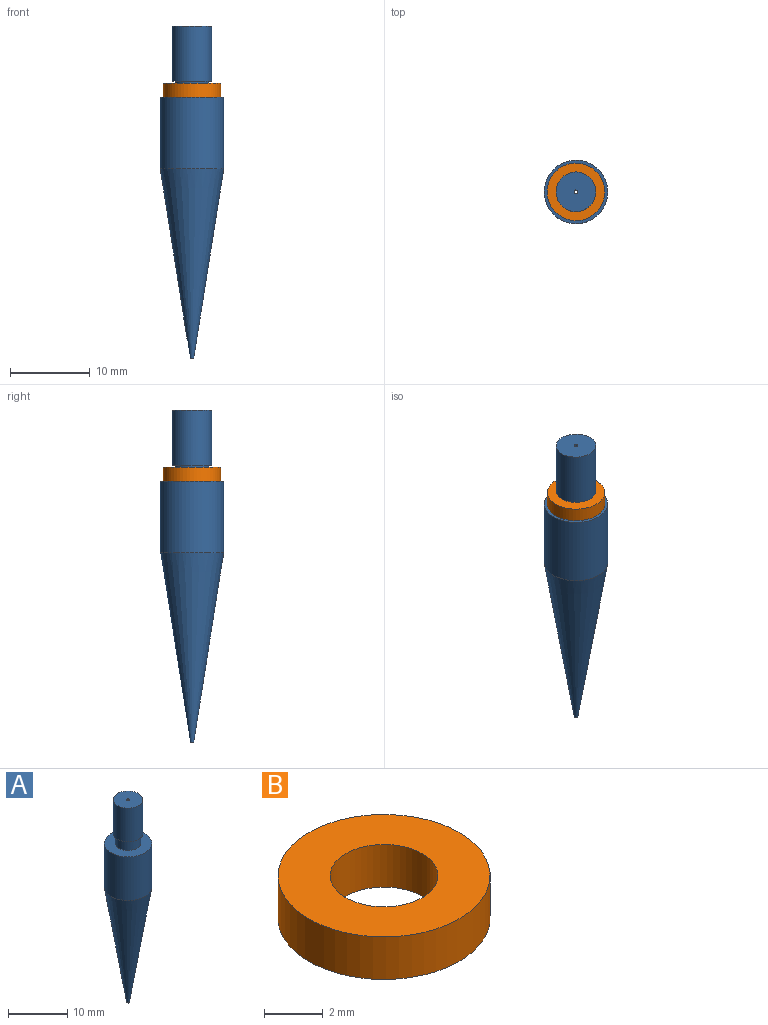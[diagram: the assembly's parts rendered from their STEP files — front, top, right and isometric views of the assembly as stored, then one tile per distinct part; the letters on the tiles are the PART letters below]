
ASSEMBLY  parts=2 mates=1
PART A: 8 faces, bbox 8x8x41.8 mm
  f0: plane 5x5mm, normal (0,0,1), area 19.5mm2, adj f6,f7
  f1: cone r=3.99mm half-angle=9deg, axis (0,0,1), area 319.3mm2, adj f2,f7
  f2: cylinder r=3.99mm len=8.99mm, axis (0,0,1), area 225.7mm2, adj f1,f3
  f3: plane 7.99x7.99mm, normal (0,0,1), area 35.8mm2, adj f2,f4
  f4: cylinder r=2.14mm len=4.27mm, axis (0,0,1), area 27.3mm2, adj f3,f5
  f5: plane 5x5mm, normal (0,0,-1), area 5.3mm2, adj f4,f6
  f6: cylinder r=2.5mm len=6.96mm, axis (0,0,1), area 109.3mm2, adj f0,f5
  f7: cylinder r=0.23mm len=41.76mm, axis (0,0,1), area 60mm2, adj f0,f1
PART B: 4 faces, bbox 7.2x7.2x1.8 mm
  f0: cylinder r=1.84mm len=3.68mm, axis (0,0,-1), area 20.6mm2, adj f2,f3
  f1: cylinder r=3.62mm len=7.24mm, axis (0,0,-1), area 40.4mm2, adj f2,f3
  f2: plane 7.24x7.24mm, normal (0,0,1), area 30.5mm2, adj f0,f1
  f3: plane 7.24x7.24mm, normal (0,0,-1), area 30.5mm2, adj f0,f1
PLACE A at identity
PLACE B t=(0,0,-8.99)mm
MATE fastened B.f1 <-> A.f1  axis (0,0,-1) through (0,0,-8.99)mm
